# Revit family: Søjle - SØ
name_source: partatom
category: Structural Columns
units: mm (PartAtom-declared; Revit-internal decimal feet)

## family parameters
Always export as geometry = No
Beam cutback in plan = From bounding box
Cut with Voids When Loaded = No
Material for Model Behavior = Other
OmniClass Number = 23.25.30.11.14.11
OmniClass Title = Columns
Section Shape = Not Defined
Shared = No
Show family pre-cut in plan views = Yes

## types (15) — shared parameters
Manufacturer = CRH Concrete
Model = SØ

## per-type parameters (varying)
| type | Diameter |
| SØ 20 | 200 mm  [stored 0.656168 ft] |
| SØ 23 | 230 mm  [stored 0.754593 ft] |
| SØ 25 | 250 mm  [stored 0.82021 ft] |
| SØ 28 | 280 mm  [stored 0.918635 ft] |
| SØ 30 | 300 mm |
| SØ 32 | 320 mm  [stored 1.04987 ft] |
| SØ 35 | 350 mm  [stored 1.14829 ft] |
| SØ 36 | 360 mm  [stored 1.1811 ft] |
| SØ 40 | 400 mm  [stored 1.31234 ft] |
| SØ 42 | 420 mm  [stored 1.37795 ft] |
| SØ 45 | 450 mm  [stored 1.47638 ft] |
| SØ 50 | 500 mm  [stored 1.64042 ft] |
| SØ 60 | 600 mm |
| SØ 65 | 650 mm  [stored 2.13255 ft] |
| SØ 70 | 700 mm  [stored 2.29659 ft] |

note: [stored X ft] marks values corroborated as IEEE doubles in the binary element streams (Revit-internal decimal feet)

## geometry (parser evidence)
native form markers: Sweep x13
no freeform markers — native parametric forms only
